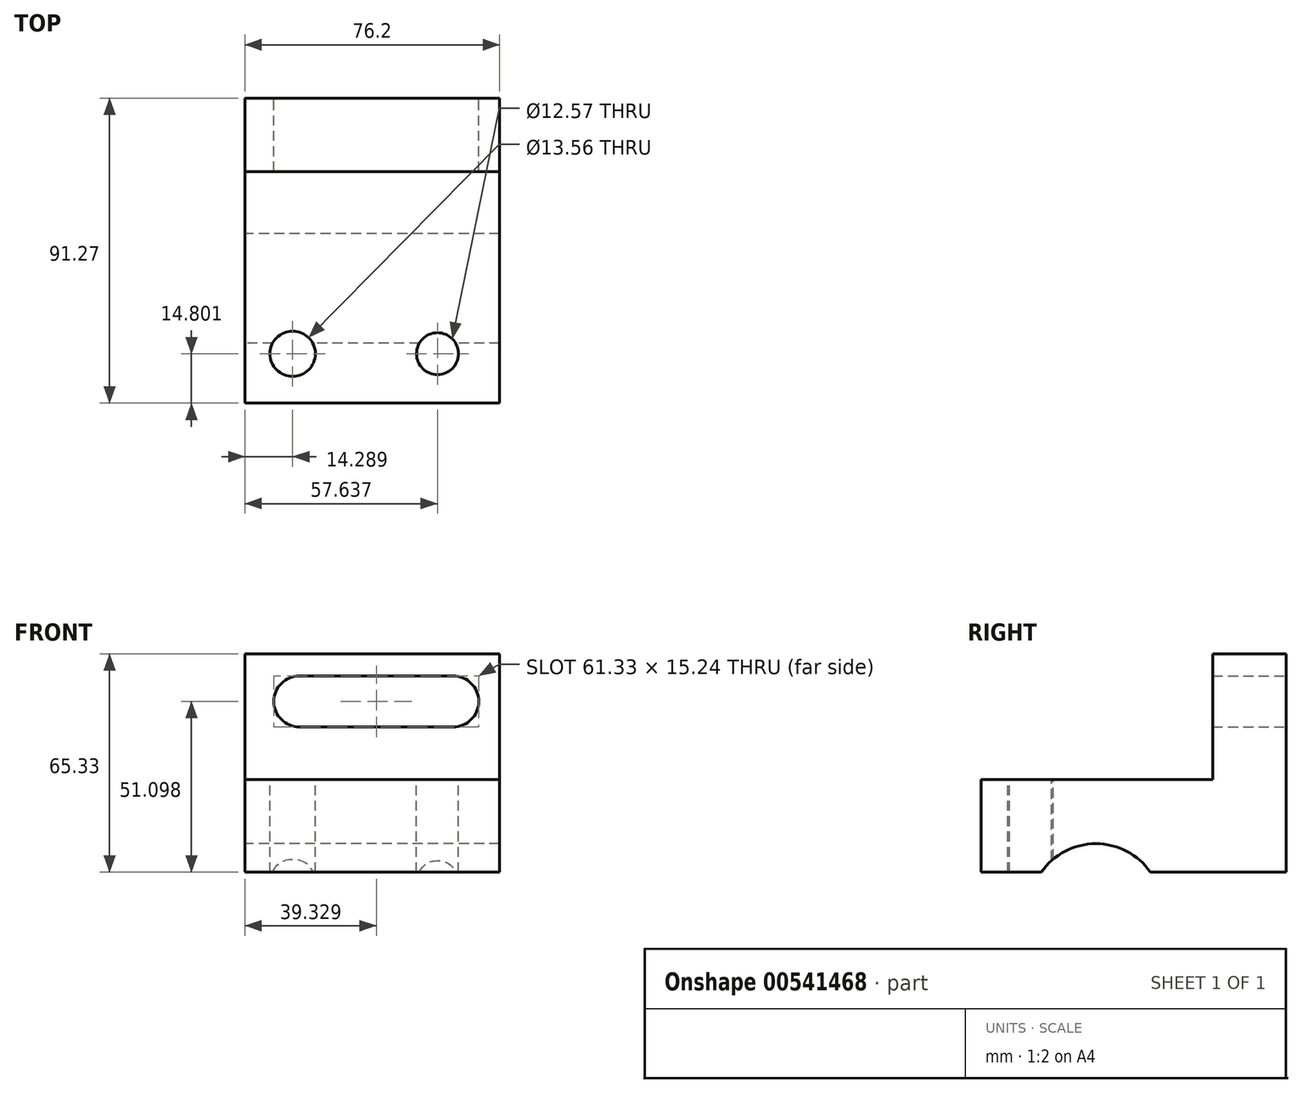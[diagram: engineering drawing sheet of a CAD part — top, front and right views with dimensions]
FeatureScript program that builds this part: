
annotation { "Feature Type Name" : "Feature", "Feature Type Description" : "" }
export const myFeature = defineFeature(function(context is Context, id is Id, definition is map)
    precondition{}
    {
        {
            var Q0;
            Q0=qCreatedBy(makeId("Right.planeOp"),FACE);
            var sketch = newSketch(context, id + "F0", { "sketchPlane" : qUnion([Q0])});
            skArc(sketch, "E0", {"start": v(0, 0) * mm, "mid": v(-16.33, 8.55) * mm, "end": v(-32.66, 0) * mm});
            skLineSegment(sketch, "E1", {"start": v(-32.66, 0) * mm, "end": v(-50.67, 0) * mm});
            skLineSegment(sketch, "E2", {"start": v(-50.67, 0) * mm, "end": v(-50.67, 27.78) * mm});
            skLineSegment(sketch, "E3", {"start": v(-50.67, 27.78) * mm, "end": v(18.62, 27.78) * mm});
            skLineSegment(sketch, "E4", {"start": v(0, 0) * mm, "end": v(18.62, 0) * mm});
            skLineSegment(sketch, "E5", {"start": v(18.62, 0) * mm, "end": v(40.6, 0) * mm});
            skLineSegment(sketch, "E6", {"start": v(40.6, 0) * mm, "end": v(40.6, 65.33) * mm});
            skLineSegment(sketch, "E7", {"start": v(40.6, 65.33) * mm, "end": v(18.62, 65.33) * mm});
            skLineSegment(sketch, "E8", {"start": v(18.62, 65.33) * mm, "end": v(18.62, 27.78) * mm});
            skSolve(sketch);
        }
        {
            var Q0;
            Q0=makeQuery(id+"F0.imprint","IMPRINT",FACE,{"disambiguationData":[TD([[makeQuery(id+"F0.imprint","IMPRINT",EDGE,{"derivedFrom":sQuery(id+"F0.wireOp",EDGE,"E0")}),-1.0]])]});
            extrude(context, id + "F1", {"entities" : qUnion([Q0]), "depth" : 76.2 * mm, "offsetDistance" : 25.4 * mm});
        }
        {
            var Q0;
            Q0=makeQuery(id+"F1.opExtrude","SWEPT_FACE",FACE,{"disambiguationData":[OSD([sQuery(id+"F0.wireOp",EDGE,"E3")])]});
            var sketch = newSketch(context, id + "F2", { "sketchPlane" : qUnion([Q0])});
            skCircle(sketch, "E9", {"center": v(14.29, -35.87) * mm, "radius": 6.78 * mm});
            skCircle(sketch, "E10", {"center": v(57.64, -35.87) * mm, "radius": 6.29 * mm});
            skSolve(sketch);
        }
        {
            var Q0;
            Q0 = qSketchRegion(id + "F2", true);
            extrude(context, id + "F3", {"entities" : qUnion([Q0]), "operationType" : NewBodyOperationType.REMOVE, "oppositeDirection" : true, "depth" : 63.25 * mm, "offsetDistance" : 25.4 * mm});
        }
        {
            var Q0;
            Q0=makeQuery(id+"F1.opExtrude","SWEPT_FACE",FACE,{"disambiguationData":[OSD([sQuery(id+"F0.wireOp",EDGE,"E6")])]});
            var sketch = newSketch(context, id + "F4", { "sketchPlane" : qUnion([Q0])});
            skArc(sketch, "E11", {"start": v(-62.37, 58.72) * mm, "mid": v(-70, 51.1) * mm, "end": v(-62.37, 43.48) * mm});
            skArc(sketch, "E12", {"start": v(-16.29, 43.48) * mm, "mid": v(-8.67, 51.1) * mm, "end": v(-16.29, 58.72) * mm});
            skLineSegment(sketch, "E13", {"start": v(-62.37, 58.72) * mm, "end": v(-16.29, 58.72) * mm});
            skLineSegment(sketch, "E14", {"start": v(-62.37, 43.48) * mm, "end": v(-16.29, 43.48) * mm});
            skSolve(sketch);
        }
        {
            var Q0;
            Q0 = qSketchRegion(id + "F4", true);
            extrude(context, id + "F5", {"entities" : qUnion([Q0]), "operationType" : NewBodyOperationType.REMOVE, "oppositeDirection" : true, "depth" : 25.4 * mm, "offsetDistance" : 25.4 * mm});
        }
    });
